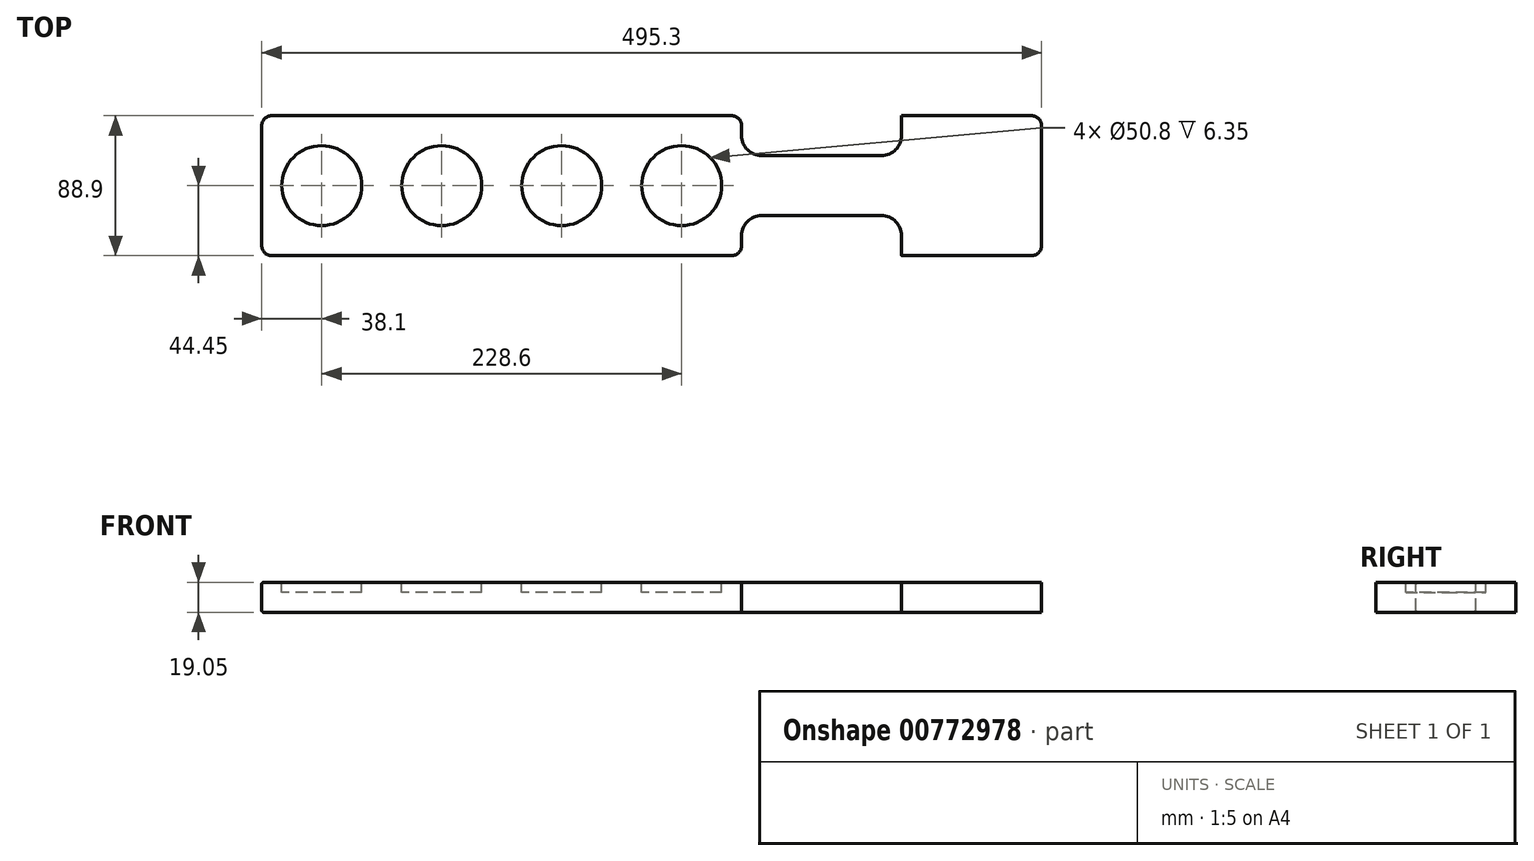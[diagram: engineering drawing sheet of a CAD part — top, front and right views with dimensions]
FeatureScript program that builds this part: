
annotation { "Feature Type Name" : "Feature", "Feature Type Description" : "" }
export const myFeature = defineFeature(function(context is Context, id is Id, definition is map)
    precondition{}
    {
        {
            var Q0;
            Q0=qCreatedBy(makeId("Top.planeOp"),FACE);
            var sketch = newSketch(context, id + "F0", { "sketchPlane" : qUnion([Q0])});
            skLineSegment(sketch, "E0.bottom", {"start": v(247.65, -44.45) * mm, "end": v(-247.65, -44.45) * mm});
            skLineSegment(sketch, "E0.top", {"start": v(247.65, 44.45) * mm, "end": v(-247.65, 44.45) * mm});
            skLineSegment(sketch, "E0.left", {"start": v(247.65, -44.45) * mm, "end": v(247.65, 44.45) * mm});
            skLineSegment(sketch, "E0.right", {"start": v(-247.65, -44.45) * mm, "end": v(-247.65, 44.45) * mm});
            skPoint(sketch, "E0.middle", {"position": v(0, 0) * mm});
            skSolve(sketch);
        }
        {
            var Q0;
            Q0=makeQuery(id+"F0.imprint","IMPRINT",FACE,{"disambiguationData":[TD([[makeQuery(id+"F0.imprint","IMPRINT",EDGE,{"derivedFrom":sQuery(id+"F0.wireOp",EDGE,"E0.bottom")}),-1.0]])]});
            extrude(context, id + "F1", {"entities" : qUnion([Q0]), "depth" : 19.05 * mm, "offsetDistance" : 25.4 * mm});
        }
        {
            var Q0;
            Q0=makeQuery(id+"F1.opExtrude","CAP_FACE",FACE,{"disambiguationData":[OSD([sQuery(id+"F0.wireOp",EDGE,"E0.bottom"),sQuery(id+"F0.wireOp",EDGE,"E0.top"),sQuery(id+"F0.wireOp",EDGE,"E0.left"),sQuery(id+"F0.wireOp",EDGE,"E0.right")])],"isStart":false});
            var sketch = newSketch(context, id + "F2", { "sketchPlane" : qUnion([Q0])});
            skLineSegment(sketch, "E1.bottom", {"start": v(57.15, 44.45) * mm, "end": v(158.75, 44.45) * mm});
            skLineSegment(sketch, "E1.top", {"start": v(57.15, 19.05) * mm, "end": v(158.75, 19.05) * mm});
            skLineSegment(sketch, "E1.left", {"start": v(57.15, 44.45) * mm, "end": v(57.15, 19.05) * mm});
            skLineSegment(sketch, "E1.right", {"start": v(158.75, 44.45) * mm, "end": v(158.75, 19.05) * mm});
            skLineSegment(sketch, "E2", {"start": v(247.65, 0) * mm, "end": v(0, 0) * mm, "construction": true});
            skLineSegment(sketch, "E3.MirrorCS", {"start": v(158.75, -44.45) * mm, "end": v(158.75, -19.05) * mm});
            skLineSegment(sketch, "E4.MirrorCS", {"start": v(57.15, -44.45) * mm, "end": v(57.15, -19.05) * mm});
            skLineSegment(sketch, "E5.MirrorCS", {"start": v(57.15, -19.05) * mm, "end": v(158.75, -19.05) * mm});
            skLineSegment(sketch, "E6.MirrorCS", {"start": v(57.15, -44.45) * mm, "end": v(158.75, -44.45) * mm});
            skSolve(sketch);
        }
        {
            var Q0;
            Q0=makeQuery(id+"F2.imprint","IMPRINT",FACE,{"disambiguationData":[TD([[makeQuery(id+"F2.imprint","IMPRINT",EDGE,{"derivedFrom":sQuery(id+"F2.wireOp",EDGE,"E3.MirrorCS")}),1.0]])]});
            var Q1;
            Q1=makeQuery(id+"F2.imprint","IMPRINT",FACE,{"disambiguationData":[TD([[makeQuery(id+"F2.imprint","IMPRINT",EDGE,{"derivedFrom":sQuery(id+"F2.wireOp",EDGE,"E1.bottom")}),1.0]])]});
            extrude(context, id + "F3", {"entities" : qUnion([Q0, Q1]), "operationType" : NewBodyOperationType.REMOVE, "endBound" : BoundingType.UP_TO_NEXT, "oppositeDirection" : true, "depth" : 25.4 * mm, "offsetDistance" : 25.4 * mm});
        }
        {
            var Q0;
            Q0=makeQuery(id+"F1.opExtrude","SWEPT_EDGE",EDGE,{"disambiguationData":[OSD([sQuery(id+"F0.wireOp",EDGE,"E0.bottom"),sQuery(id+"F0.wireOp",EDGE,"E0.right")])]});
            var Q1;
            Q1=makeQuery(id+"F3.boolean.opBoolean","COPY",EDGE,{"derivedFrom":makeQuery(id+"F3.opExtrude","SWEPT_EDGE",EDGE,{"disambiguationData":[OSD([sQuery(id+"F0.wireOp",EDGE,"E0.bottom"),sQuery(id+"F2.wireOp",EDGE,"E4.MirrorCS"),sQuery(id+"F2.wireOp",EDGE,"E6.MirrorCS")])]})});
            var Q2;
            Q2=makeQuery(id+"F1.opExtrude","SWEPT_EDGE",EDGE,{"disambiguationData":[OSD([sQuery(id+"F0.wireOp",EDGE,"E0.top"),sQuery(id+"F0.wireOp",EDGE,"E0.right")])]});
            var Q3;
            Q3=makeQuery(id+"F3.boolean.opBoolean","COPY",EDGE,{"derivedFrom":makeQuery(id+"F3.opExtrude","SWEPT_EDGE",EDGE,{"disambiguationData":[OSD([sQuery(id+"F0.wireOp",EDGE,"E0.top"),sQuery(id+"F2.wireOp",EDGE,"E1.bottom"),sQuery(id+"F2.wireOp",EDGE,"E1.left")])]})});
            var Q4;
            Q4=makeQuery(id+"F3.boolean.opBoolean","COPY",EDGE,{"derivedFrom":makeQuery(id+"F3.opExtrude","SWEPT_EDGE",EDGE,{"disambiguationData":[OSD([sQuery(id+"F0.wireOp",EDGE,"E0.top"),sQuery(id+"F2.wireOp",EDGE,"E1.bottom"),sQuery(id+"F2.wireOp",EDGE,"E1.right")])]})});
            var Q5;
            Q5=makeQuery(id+"F3.boolean.opBoolean","COPY",EDGE,{"derivedFrom":makeQuery(id+"F3.opExtrude","SWEPT_EDGE",EDGE,{"disambiguationData":[OSD([sQuery(id+"F0.wireOp",EDGE,"E0.bottom"),sQuery(id+"F2.wireOp",EDGE,"E3.MirrorCS"),sQuery(id+"F2.wireOp",EDGE,"E6.MirrorCS")])]})});
            var Q6;
            Q6=makeQuery(id+"F1.opExtrude","SWEPT_EDGE",EDGE,{"disambiguationData":[OSD([sQuery(id+"F0.wireOp",EDGE,"E0.bottom"),sQuery(id+"F0.wireOp",EDGE,"E0.left")])]});
            var Q7;
            Q7=makeQuery(id+"F1.opExtrude","SWEPT_EDGE",EDGE,{"disambiguationData":[OSD([sQuery(id+"F0.wireOp",EDGE,"E0.top"),sQuery(id+"F0.wireOp",EDGE,"E0.left")])]});
            fillet(context, id + "F4", {"entities" : qUnion([Q0, Q1, Q2, Q3, Q4, Q5, Q6, Q7]), "radius" : 6.35 * mm, "tangentPropagation" : true, "allowEdgeOverflow" : false});
        }
        {
            var Q0;
            Q0=makeQuery(id+"F3.boolean.opBoolean","COPY",EDGE,{"derivedFrom":makeQuery(id+"F3.opExtrude","SWEPT_EDGE",EDGE,{"disambiguationData":[OSD([sQuery(id+"F2.wireOp",EDGE,"E4.MirrorCS"),sQuery(id+"F2.wireOp",EDGE,"E5.MirrorCS")])]})});
            var Q1;
            Q1=makeQuery(id+"F3.boolean.opBoolean","COPY",EDGE,{"derivedFrom":makeQuery(id+"F3.opExtrude","SWEPT_EDGE",EDGE,{"disambiguationData":[OSD([sQuery(id+"F2.wireOp",EDGE,"E1.top"),sQuery(id+"F2.wireOp",EDGE,"E1.left")])]})});
            var Q2;
            Q2=makeQuery(id+"F3.boolean.opBoolean","COPY",EDGE,{"derivedFrom":makeQuery(id+"F3.opExtrude","SWEPT_EDGE",EDGE,{"disambiguationData":[OSD([sQuery(id+"F2.wireOp",EDGE,"E1.top"),sQuery(id+"F2.wireOp",EDGE,"E1.right")])]})});
            var Q3;
            Q3=makeQuery(id+"F3.boolean.opBoolean","COPY",EDGE,{"derivedFrom":makeQuery(id+"F3.opExtrude","SWEPT_EDGE",EDGE,{"disambiguationData":[OSD([sQuery(id+"F2.wireOp",EDGE,"E3.MirrorCS"),sQuery(id+"F2.wireOp",EDGE,"E5.MirrorCS")])]})});
            fillet(context, id + "F5", {"entities" : qUnion([Q0, Q1, Q2, Q3]), "radius" : 12.7 * mm, "tangentPropagation" : true, "allowEdgeOverflow" : false});
        }
        {
            var Q0;
            Q0=makeQuery(id+"F1.opExtrude","CAP_FACE",FACE,{"disambiguationData":[OSD([sQuery(id+"F0.wireOp",EDGE,"E0.bottom"),sQuery(id+"F0.wireOp",EDGE,"E0.top"),sQuery(id+"F0.wireOp",EDGE,"E0.left"),sQuery(id+"F0.wireOp",EDGE,"E0.right")])],"isStart":false});
            var sketch = newSketch(context, id + "F6", { "sketchPlane" : qUnion([Q0])});
            skCircle(sketch, "E7", {"center": v(-209.55, 0) * mm, "radius": 25.4 * mm});
            skCircle(sketch, "E8.1.0.0", {"center": v(-133.35, 0) * mm, "radius": 25.4 * mm});
            skCircle(sketch, "E8.2.0.0", {"center": v(-57.15, 0) * mm, "radius": 25.4 * mm});
            skCircle(sketch, "E8.3.0.0", {"center": v(19.05, 0) * mm, "radius": 25.4 * mm});
            skLineSegment(sketch, "E8.direction1", {"start": v(-209.55, 0) * mm, "end": v(-133.35, 0) * mm, "construction": true});
            skSolve(sketch);
        }
        {
            var Q0;
            Q0 = qSketchRegion(id + "F6", true);
            extrude(context, id + "F7", {"entities" : qUnion([Q0]), "operationType" : NewBodyOperationType.REMOVE, "oppositeDirection" : true, "depth" : 6.35 * mm, "offsetDistance" : 25.4 * mm});
        }
        {
            var Q0;
            {var subQ0=sQuery(id+"F0.wireOp",EDGE,"E0.bottom");var subQ1=sQuery(id+"F0.wireOp",EDGE,"E0.right");Q0=makeQuery(id+"F3.boolean.opBoolean","SPLIT",EDGE,{"disambiguationData":[TD([makeQuery(id+"F1.opExtrude","SWEPT_FACE",FACE,{"disambiguationData":[OSD([subQ1])]})])],"derivedFrom":makeQuery(id+"F1.opExtrude","CAP_EDGE",EDGE,{"disambiguationData":[OSD([subQ0])],"isStart":false})});}
            var Q1;
            {var subQ0=sQuery(id+"F0.wireOp",EDGE,"E0.bottom");var subQ1=sQuery(id+"F0.wireOp",EDGE,"E0.right");Q1=makeQuery(id+"F3.boolean.opBoolean","SPLIT",EDGE,{"disambiguationData":[TD([makeQuery(id+"F1.opExtrude","SWEPT_FACE",FACE,{"disambiguationData":[OSD([subQ1])]})])],"derivedFrom":makeQuery(id+"F1.opExtrude","CAP_EDGE",EDGE,{"disambiguationData":[OSD([subQ0])],"isStart":true})});}
            fillet(context, id + "F8", {"entities" : qUnion([Q0, Q1]), "radius" : 1.27 * mm, "tangentPropagation" : true, "allowEdgeOverflow" : false});
        }
    });
